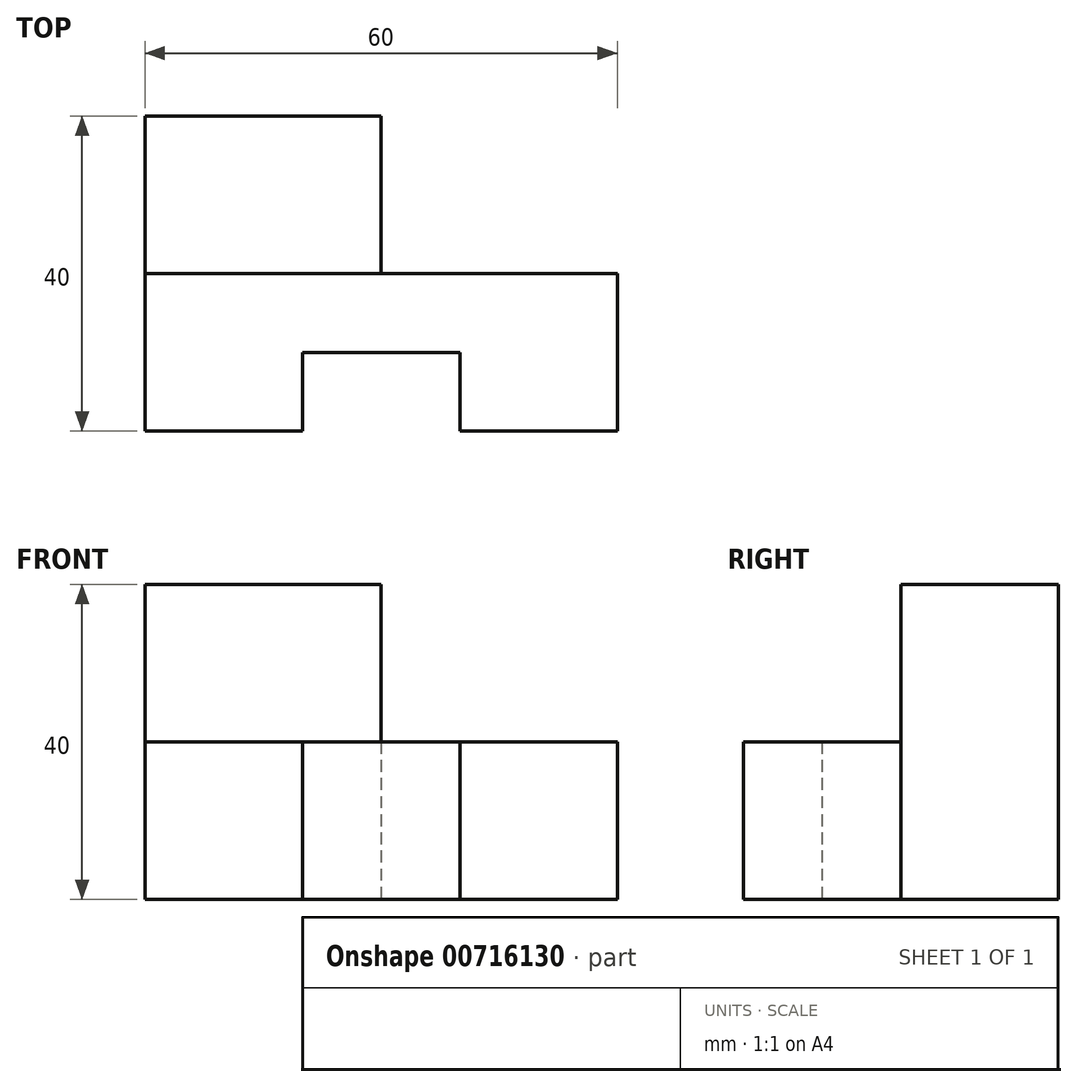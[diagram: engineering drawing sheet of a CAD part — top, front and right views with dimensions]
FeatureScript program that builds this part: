
annotation { "Feature Type Name" : "Feature", "Feature Type Description" : "" }
export const myFeature = defineFeature(function(context is Context, id is Id, definition is map)
    precondition{}
    {
        {
            var Q0;
            Q0=qCreatedBy(makeId("Top.planeOp"),FACE);
            var sketch = newSketch(context, id + "F0", { "sketchPlane" : qUnion([Q0])});
            skLineSegment(sketch, "E0", {"start": v(0, 0) * mm, "end": v(0, 20) * mm});
            skLineSegment(sketch, "E1", {"start": v(0, 20) * mm, "end": v(-60, 20) * mm});
            skLineSegment(sketch, "E2", {"start": v(-60, 20) * mm, "end": v(-60, 0) * mm});
            skLineSegment(sketch, "E3", {"start": v(-60, 0) * mm, "end": v(-40, 0) * mm});
            skLineSegment(sketch, "E4", {"start": v(-40, 0) * mm, "end": v(-40, 10) * mm});
            skLineSegment(sketch, "E5", {"start": v(-40, 10) * mm, "end": v(-20, 10) * mm});
            skLineSegment(sketch, "E6", {"start": v(-20, 10) * mm, "end": v(-20, 0) * mm});
            skLineSegment(sketch, "E7", {"start": v(-20, 0) * mm, "end": v(0, 0) * mm});
            skSolve(sketch);
        }
        {
            var Q0;
            Q0 = qSketchRegion(id + "F0", true);
            extrude(context, id + "F1", {"entities" : qUnion([Q0]), "depth" : 20 * mm, "offsetDistance" : 25 * mm});
        }
        {
            var Q0;
            Q0=makeQuery(id+"F1.opExtrude","CAP_FACE",FACE,{"disambiguationData":[OSD([sQuery(id+"F0.wireOp",EDGE,"E0"),sQuery(id+"F0.wireOp",EDGE,"E1"),sQuery(id+"F0.wireOp",EDGE,"E2"),sQuery(id+"F0.wireOp",EDGE,"E3"),sQuery(id+"F0.wireOp",EDGE,"E4"),sQuery(id+"F0.wireOp",EDGE,"E5"),sQuery(id+"F0.wireOp",EDGE,"E6"),sQuery(id+"F0.wireOp",EDGE,"E7")])],"isStart":true});
            var sketch = newSketch(context, id + "F2", { "sketchPlane" : qUnion([Q0])});
            skLineSegment(sketch, "E8.bottom", {"start": v(-60, -20) * mm, "end": v(-30, -20) * mm});
            skLineSegment(sketch, "E8.top", {"start": v(-60, -40) * mm, "end": v(-30, -40) * mm});
            skLineSegment(sketch, "E8.left", {"start": v(-60, -20) * mm, "end": v(-60, -40) * mm});
            skLineSegment(sketch, "E8.right", {"start": v(-30, -20) * mm, "end": v(-30, -40) * mm});
            skSolve(sketch);
        }
        {
            var Q0;
            Q0=makeQuery(id+"F2.imprint","IMPRINT",FACE,{"disambiguationData":[TD([[makeQuery(id+"F2.imprint","IMPRINT",EDGE,{"derivedFrom":sQuery(id+"F2.wireOp",EDGE,"E8.bottom")}),1.0]])]});
            extrude(context, id + "F3", {"entities" : qUnion([Q0]), "operationType" : NewBodyOperationType.ADD, "oppositeDirection" : true, "depth" : 40 * mm, "offsetDistance" : 25 * mm});
        }
    });
